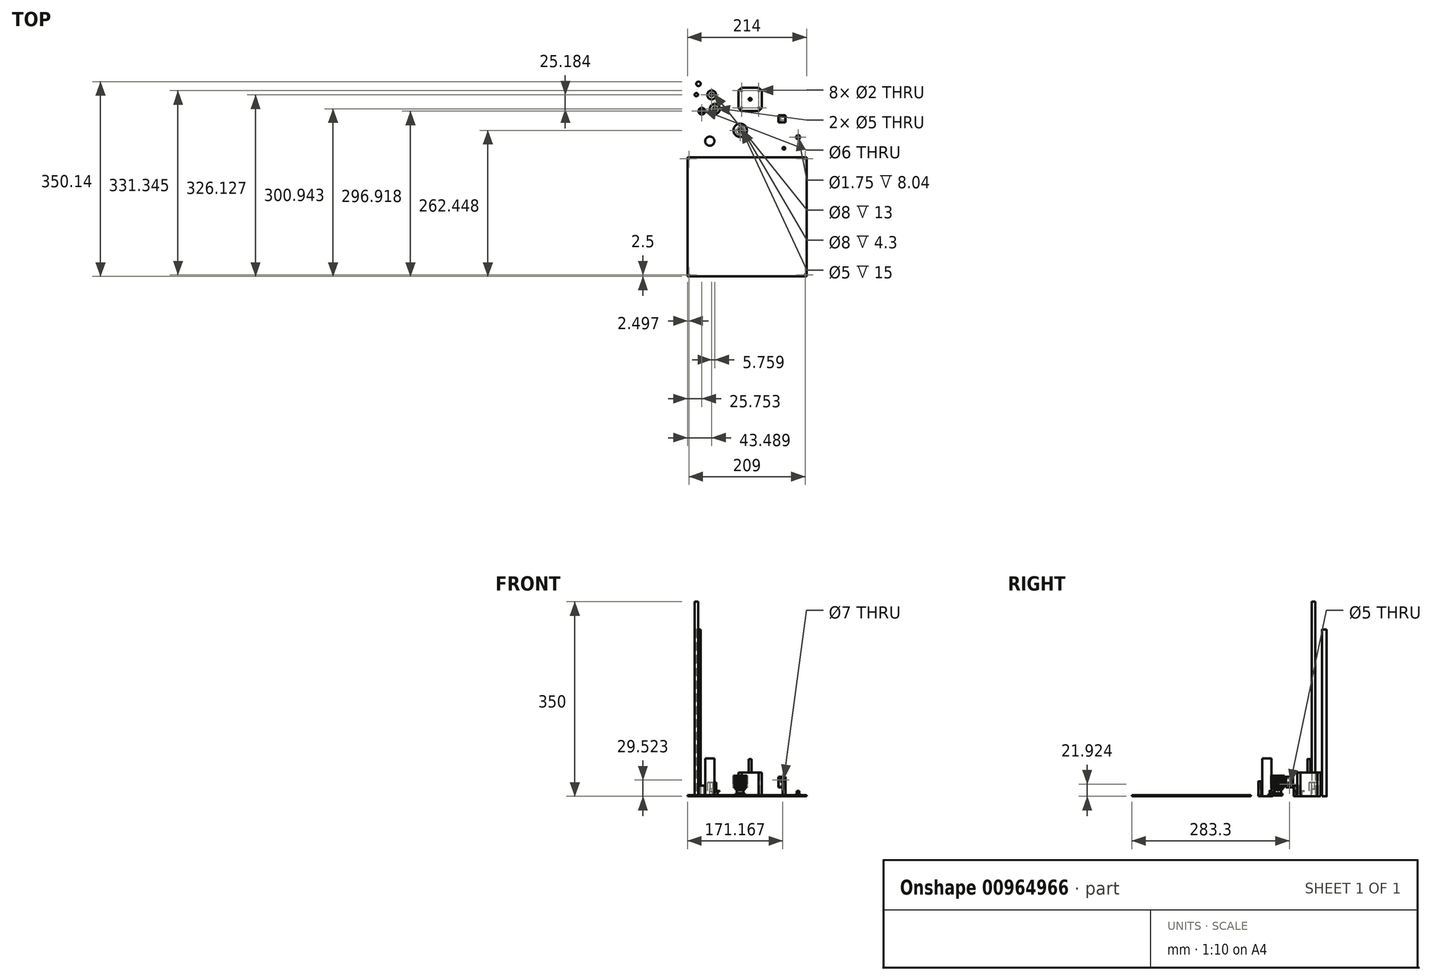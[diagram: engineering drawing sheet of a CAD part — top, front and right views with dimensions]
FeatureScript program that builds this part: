
annotation { "Feature Type Name" : "Feature", "Feature Type Description" : "" }
export const myFeature = defineFeature(function(context is Context, id is Id, definition is map)
    precondition{}
    {
        {
            var Q0;
            Q0=qCreatedBy(makeId("Top.planeOp"),FACE);
            var sketch = newSketch(context, id + "F0", { "sketchPlane" : qUnion([Q0])});
            skCircle(sketch, "E0", {"center": v(-57.26, 36.88) * mm, "radius": 3 * mm});
            skSolve(sketch);
        }
        {
            var Q0;
            Q0=makeQuery(id+"F0.imprint","IMPRINT",FACE,{"disambiguationData":[TD([[makeQuery(id+"F0.imprint","IMPRINT",EDGE,{"derivedFrom":sQuery(id+"F0.wireOp",EDGE,"E0")}),1.0]])]});
            extrude(context, id + "F1", {"entities" : qUnion([Q0]), "depth" : 350 * mm, "offsetDistance" : 25 * mm});
        }
        {
            var Q0;
            Q0=qCreatedBy(makeId("Top.planeOp"),FACE);
            var sketch = newSketch(context, id + "F2", { "sketchPlane" : qUnion([Q0])});
            skCircle(sketch, "E1", {"center": v(-29.78, 36.48) * mm, "radius": 4 * mm});
            skCircle(sketch, "E2", {"center": v(-29.78, 36.48) * mm, "radius": 8 * mm});
            skSolve(sketch);
        }
        {
            var Q0;
            Q0=makeQuery(id+"F2.imprint","IMPRINT",FACE,{"disambiguationData":[TD([[makeQuery(id+"F2.imprint","IMPRINT",EDGE,{"derivedFrom":sQuery(id+"F2.wireOp",EDGE,"E1")}),-1.0]])]});
            extrude(context, id + "F3", {"entities" : qUnion([Q0]), "depth" : 25 * mm, "offsetDistance" : 25 * mm});
        }
        {
            var Q0;
            Q0=qCreatedBy(makeId("Top.planeOp"),FACE);
            var sketch = newSketch(context, id + "F4", { "sketchPlane" : qUnion([Q0])});
            skCircle(sketch, "E3", {"center": v(-47.52, 7.27) * mm, "radius": 3 * mm});
            skCircle(sketch, "E4", {"center": v(-47.52, 7.27) * mm, "radius": 6 * mm});
            skSolve(sketch);
        }
        {
            var Q0;
            Q0=makeQuery(id+"F4.imprint","IMPRINT",FACE,{"disambiguationData":[TD([[makeQuery(id+"F4.imprint","IMPRINT",EDGE,{"derivedFrom":sQuery(id+"F4.wireOp",EDGE,"E3")}),-1.0]])]});
            extrude(context, id + "F5", {"entities" : qUnion([Q0]), "depth" : 19 * mm, "offsetDistance" : 25 * mm});
        }
        {
            var Q0;
            Q0=qCreatedBy(makeId("Top.planeOp"),FACE);
            var sketch = newSketch(context, id + "F6", { "sketchPlane" : qUnion([Q0])});
            skCircle(sketch, "E5", {"center": v(-24.02, 11.3) * mm, "radius": 5 * mm});
            skSolve(sketch);
        }
        {
            var Q0;
            Q0 = qSketchRegion(id + "F6", true);
            extrude(context, id + "F7", {"entities" : qUnion([Q0]), "depth" : 10 * mm, "offsetDistance" : 25 * mm});
        }
        {
            var Q0;
            Q0=makeQuery(id+"F7.opExtrude","CAP_FACE",FACE,{"disambiguationData":[OSD([sQuery(id+"F6.wireOp",EDGE,"E5")])],"isStart":false});
            var sketch = newSketch(context, id + "F8", { "sketchPlane" : qUnion([Q0])});
            skCircle(sketch, "E6", {"center": v(-24.02, 11.3) * mm, "radius": 5 * mm});
            skPoint(sketch, "E6.first.point", {"position": v(-22.8, 16.14) * mm});
            skPoint(sketch, "E6.second.point", {"position": v(-28.66, 13.17) * mm});
            skPoint(sketch, "E6.third.point", {"position": v(-23.1, 6.38) * mm});
            skCircle(sketch, "E7", {"center": v(-24.02, 11.3) * mm, "radius": 9 * mm});
            skSolve(sketch);
        }
        {
            var Q0;
            Q0 = qSketchRegion(id + "F8", true);
            extrude(context, id + "F9", {"entities" : qUnion([Q0]), "operationType" : NewBodyOperationType.ADD, "oppositeDirection" : true, "depth" : 1 * mm, "offsetDistance" : 25 * mm});
        }
        {
            var Q0;
            Q0=makeQuery(id+"F7.opExtrude","CAP_FACE",FACE,{"disambiguationData":[OSD([sQuery(id+"F6.wireOp",EDGE,"E5")])],"isStart":true});
            var sketch = newSketch(context, id + "F10", { "sketchPlane" : qUnion([Q0])});
            skPoint(sketch, "E8.first.point", {"position": v(-20.18, -8.1) * mm});
            skPoint(sketch, "E8.second.point", {"position": v(-24.93, -6.38) * mm});
            skPoint(sketch, "E8.third.point", {"position": v(-24.94, -16.4) * mm});
            skCircle(sketch, "E9", {"center": v(-24.06, -11.38) * mm, "radius": 9 * mm});
            skSolve(sketch);
        }
        {
            var Q0;
            Q0 = qSketchRegion(id + "F10", true);
            extrude(context, id + "F11", {"entities" : qUnion([Q0]), "operationType" : NewBodyOperationType.ADD, "oppositeDirection" : true, "depth" : 1 * mm, "offsetDistance" : 25 * mm});
        }
        {
            var Q0;
            Q0=qCreatedBy(makeId("Top.planeOp"),FACE);
            var sketch = newSketch(context, id + "F12", { "sketchPlane" : qUnion([Q0])});
            skLineSegment(sketch, "E10.bottom", {"start": v(23.86, 49.7) * mm, "end": v(54.86, 49.7) * mm});
            skLineSegment(sketch, "E10.top", {"start": v(23.86, 7.7) * mm, "end": v(54.86, 7.7) * mm});
            skLineSegment(sketch, "E11", {"start": v(38.86, 49.7) * mm, "end": v(54.86, 49.7) * mm, "construction": true});
            skLineSegment(sketch, "E12", {"start": v(38.86, 49.7) * mm, "end": v(23.86, 49.7) * mm, "construction": true});
            skLineSegment(sketch, "E13", {"start": v(23.86, 49.7) * mm, "end": v(23.86, 7.7) * mm, "construction": true});
            skLineSegment(sketch, "E14", {"start": v(23.86, 7.7) * mm, "end": v(54.86, 7.7) * mm, "construction": true});
            skLineSegment(sketch, "E15", {"start": v(54.86, 7.7) * mm, "end": v(54.86, 49.7) * mm, "construction": true});
            skLineSegment(sketch, "E16", {"start": v(54.86, 49.7) * mm, "end": v(54.86, 44.2) * mm, "construction": true});
            skLineSegment(sketch, "E17", {"start": v(54.86, 44.2) * mm, "end": v(60.36, 44.2) * mm, "construction": true});
            skLineSegment(sketch, "E18", {"start": v(60.36, 44.2) * mm, "end": v(18.36, 44.2) * mm, "construction": true});
            skLineSegment(sketch, "E19", {"start": v(18.36, 13.2) * mm, "end": v(60.36, 13.2) * mm, "construction": true});
            skCircle(sketch, "E20", {"center": v(23.86, 44.2) * mm, "radius": 1 * mm});
            skLineSegment(sketch, "E21", {"start": v(23.86, 49.7) * mm, "end": v(18.36, 44.2) * mm});
            skLineSegment(sketch, "E22", {"start": v(54.86, 49.7) * mm, "end": v(60.36, 44.2) * mm});
            skLineSegment(sketch, "E23", {"start": v(60.36, 13.2) * mm, "end": v(54.86, 7.7) * mm});
            skLineSegment(sketch, "E24", {"start": v(18.36, 13.2) * mm, "end": v(23.86, 7.7) * mm});
            skCircle(sketch, "E25", {"center": v(23.86, 13.2) * mm, "radius": 1 * mm});
            skCircle(sketch, "E26", {"center": v(54.86, 13.2) * mm, "radius": 1 * mm});
            skCircle(sketch, "E27", {"center": v(54.86, 44.2) * mm, "radius": 1 * mm});
            skPoint(sketch, "E28.orphan", {"position": v(18.36, 49.7) * mm});
            skPoint(sketch, "E29.orphan", {"position": v(59.36, 49.7) * mm});
            skPoint(sketch, "E30.orphan", {"position": v(59.36, 7.7) * mm});
            skPoint(sketch, "E31.orphan", {"position": v(18.36, 7.7) * mm});
            skLineSegment(sketch, "E32", {"start": v(18.36, 44.2) * mm, "end": v(18.36, 13.2) * mm});
            skLineSegment(sketch, "E33", {"start": v(60.36, 44.2) * mm, "end": v(60.36, 13.2) * mm});
            skLineSegment(sketch, "E34", {"start": v(23.86, 44.2) * mm, "end": v(54.86, 44.2) * mm, "construction": true});
            skLineSegment(sketch, "E35", {"start": v(23.86, 44.2) * mm, "end": v(18.36, 44.2) * mm, "construction": true});
            skLineSegment(sketch, "E36", {"start": v(23.86, 44.2) * mm, "end": v(23.86, 49.7) * mm, "construction": true});
            skLineSegment(sketch, "E37", {"start": v(23.86, 13.2) * mm, "end": v(18.36, 13.2) * mm, "construction": true});
            skLineSegment(sketch, "E38", {"start": v(23.86, 13.2) * mm, "end": v(23.86, 7.7) * mm, "construction": true});
            skLineSegment(sketch, "E39", {"start": v(54.86, 13.2) * mm, "end": v(23.86, 13.2) * mm, "construction": true});
            skLineSegment(sketch, "E40", {"start": v(54.86, 44.2) * mm, "end": v(23.86, 13.2) * mm, "construction": true});
            skCircle(sketch, "E41", {"center": v(39.36, 28.7) * mm, "radius": 2.5 * mm});
            skSolve(sketch);
        }
        {
            var Q0;
            Q0=makeQuery(id+"F12.imprint","IMPRINT",FACE,{"disambiguationData":[TD([[makeQuery(id+"F12.imprint","IMPRINT",EDGE,{"derivedFrom":sQuery(id+"F12.wireOp",EDGE,"E10.bottom")}),-1.0]])]});
            extrude(context, id + "F13", {"entities" : qUnion([Q0]), "depth" : 43 * mm, "offsetDistance" : 25 * mm});
        }
        {
            var Q0;
            Q0=makeQuery(id+"F12.imprint","IMPRINT",FACE,{"disambiguationData":[TD([[makeQuery(id+"F12.imprint","IMPRINT",EDGE,{"derivedFrom":sQuery(id+"F12.wireOp",EDGE,"E41")}),1.0]])]});
            extrude(context, id + "F14", {"entities" : qUnion([Q0]), "operationType" : NewBodyOperationType.ADD, "depth" : (42 + 25) * mm, "offsetDistance" : 25 * mm});
        }
        {
            var Q0;
            Q0=makeQuery(id+"F3.opExtrude","CAP_FACE",FACE,{"disambiguationData":[OSD([sQuery(id+"F2.wireOp",EDGE,"E1"),sQuery(id+"F2.wireOp",EDGE,"E2")])],"isStart":false});
            var sketch = newSketch(context, id + "F15", { "sketchPlane" : qUnion([Q0])});
            skCircle(sketch, "E42", {"center": v(-29.78, 36.48) * mm, "radius": 2.5 * mm});
            skSolve(sketch);
        }
        {
            var Q0;
            Q0=makeQuery(id+"F15.imprint","IMPRINT",FACE,{"disambiguationData":[TD([[makeQuery(id+"F15.imprint","IMPRINT",EDGE,{"derivedFrom":sQuery(id+"F15.wireOp",EDGE,"E42")}),-1.0]])]});
            extrude(context, id + "F16", {"entities" : qUnion([Q0]), "operationType" : NewBodyOperationType.ADD, "oppositeDirection" : true, "depth" : 12 * mm, "offsetDistance" : 25 * mm});
        }
        {
            var Q0;
            Q0=qCreatedBy(makeId("Top.planeOp"),FACE);
            var sketch = newSketch(context, id + "F17", { "sketchPlane" : qUnion([Q0])});
            skCircle(sketch, "E43", {"center": v(-53.53, 56.49) * mm, "radius": 4 * mm});
            skSolve(sketch);
        }
        {
            var Q0;
            Q0 = qSketchRegion(id + "F17", true);
            extrude(context, id + "F18", {"entities" : qUnion([Q0]), "depth" : 300 * mm, "offsetDistance" : 25 * mm});
        }
        {
            var Q0;
            Q0=qCreatedBy(makeId("Top.planeOp"),FACE);
            var sketch = newSketch(context, id + "F19", { "sketchPlane" : qUnion([Q0])});
            skLineSegment(sketch, "E44.bottom", {"start": v(-73.27, -75.65) * mm, "end": v(140.73, -75.65) * mm});
            skLineSegment(sketch, "E44.top", {"start": v(-73.27, -289.65) * mm, "end": v(140.73, -289.65) * mm});
            skLineSegment(sketch, "E44.left", {"start": v(-73.27, -75.65) * mm, "end": v(-73.27, -289.65) * mm});
            skLineSegment(sketch, "E44.right", {"start": v(140.73, -75.65) * mm, "end": v(140.73, -289.65) * mm});
            skLineSegment(sketch, "E45", {"start": v(-73.27, -75.65) * mm, "end": v(140.73, -289.65) * mm, "construction": true});
            skLineSegment(sketch, "E46.bottom", {"start": v(138.23, -78.15) * mm, "end": v(-70.77, -78.15) * mm, "construction": true});
            skLineSegment(sketch, "E46.top", {"start": v(138.23, -287.15) * mm, "end": v(-70.77, -287.15) * mm, "construction": true});
            skLineSegment(sketch, "E46.left", {"start": v(138.23, -78.15) * mm, "end": v(138.23, -287.15) * mm, "construction": true});
            skLineSegment(sketch, "E46.right", {"start": v(-70.77, -78.15) * mm, "end": v(-70.77, -287.15) * mm, "construction": true});
            skPoint(sketch, "E46.middle", {"position": v(33.73, -182.65) * mm});
            skCircle(sketch, "E47", {"center": v(-70.77, -78.15) * mm, "radius": 1 * mm});
            skCircle(sketch, "E48", {"center": v(138.23, -78.15) * mm, "radius": 1 * mm});
            skCircle(sketch, "E49", {"center": v(138.23, -287.15) * mm, "radius": 1 * mm});
            skCircle(sketch, "E50", {"center": v(-70.77, -287.15) * mm, "radius": 1 * mm});
            skSolve(sketch);
        }
        {
            var Q0;
            Q0=makeQuery(id+"F19.imprint","IMPRINT",FACE,{"disambiguationData":[TD([[makeQuery(id+"F19.imprint","IMPRINT",EDGE,{"derivedFrom":sQuery(id+"F19.wireOp",EDGE,"E44.bottom")}),-1.0]])]});
            extrude(context, id + "F20", {"entities" : qUnion([Q0]), "depth" : 2 * mm, "offsetDistance" : 25 * mm});
        }
        {
            var Q0;
            Q0=qCreatedBy(makeId("Top.planeOp"),FACE);
            var sketch = newSketch(context, id + "F21", { "sketchPlane" : qUnion([Q0])});
            skCircle(sketch, "E51", {"center": v(-33.14, -46.66) * mm, "radius": 8.25 * mm});
            skSolve(sketch);
        }
        {
            var Q0;
            Q0=makeQuery(id+"F21.imprint","IMPRINT",FACE,{"disambiguationData":[TD([[makeQuery(id+"F21.imprint","IMPRINT",EDGE,{"derivedFrom":sQuery(id+"F21.wireOp",EDGE,"E51")}),1.0]])]});
            extrude(context, id + "F22", {"entities" : qUnion([Q0]), "depth" : 68 * mm, "offsetDistance" : 25 * mm});
        }
        {
            var Q0;
            Q0=qCreatedBy(makeId("Top.planeOp"),FACE);
            var sketch = newSketch(context, id + "F23", { "sketchPlane" : qUnion([Q0])});
            skCircle(sketch, "E52", {"center": v(21.49, -27.2) * mm, "radius": 2 * mm});
            skSolve(sketch);
        }
        {
            var Q0;
            Q0 = qSketchRegion(id + "F23", true);
            extrude(context, id + "F24", {"entities" : qUnion([Q0]), "depth" : 1.7 * mm, "offsetDistance" : 25 * mm});
        }
        {
            var Q0;
            Q0=makeQuery(id+"F24.opExtrude","CAP_FACE",FACE,{"disambiguationData":[OSD([sQuery(id+"F23.wireOp",EDGE,"E52")])],"isStart":false});
            var sketch = newSketch(context, id + "F25", { "sketchPlane" : qUnion([Q0])});
            skCircle(sketch, "E53", {"center": v(21.49, -27.2) * mm, "radius": 8 * mm});
            skSolve(sketch);
        }
        {
            var Q0;
            Q0=makeQuery(id+"F25.imprint","IMPRINT",FACE,{"disambiguationData":[TD([[makeQuery(id+"F25.imprint","IMPRINT",EDGE,{"derivedFrom":sQuery(id+"F25.wireOp",EDGE,"E53")}),1.0]])]});
            var Q1;
            Q1=makeQuery(id+"F25.imprint","IMPRINT",FACE,{"disambiguationData":[TD([[makeQuery(id+"F25.imprint","IMPRINT",EDGE,{"derivedFrom":makeQuery(id+"F24.opExtrude","CAP_EDGE",EDGE,{"disambiguationData":[OSD([sQuery(id+"F23.wireOp",EDGE,"E52")])],"isStart":false})}),1.0]])]});
            extrude(context, id + "F26", {"entities" : qUnion([Q0, Q1]), "operationType" : NewBodyOperationType.ADD, "depth" : 3.7 * mm, "offsetDistance" : 25 * mm});
        }
        {
            var Q0;
            Q0=makeQuery(id+"F26.opExtrude","CAP_FACE",FACE,{"disambiguationData":[OSD([sQuery(id+"F25.wireOp",EDGE,"E53")])],"isStart":false});
            var sketch = newSketch(context, id + "F27", { "sketchPlane" : qUnion([Q0])});
            skCircle(sketch, "E54", {"center": v(21.49, -27.2) * mm, "radius": 6 * mm});
            skSolve(sketch);
        }
        {
            var Q0;
            Q0=makeQuery(id+"F27.imprint","IMPRINT",FACE,{"disambiguationData":[TD([[makeQuery(id+"F27.imprint","IMPRINT",EDGE,{"derivedFrom":sQuery(id+"F27.wireOp",EDGE,"E54")}),1.0]])]});
            extrude(context, id + "F28", {"entities" : qUnion([Q0]), "operationType" : NewBodyOperationType.ADD, "depth" : 6 * mm, "offsetDistance" : 25 * mm});
        }
        {
            var Q0;
            Q0=makeQuery(id+"F28.opExtrude","CAP_FACE",FACE,{"disambiguationData":[OSD([sQuery(id+"F27.wireOp",EDGE,"E54")])],"isStart":false});
            var sketch = newSketch(context, id + "F29", { "sketchPlane" : qUnion([Q0])});
            skCircle(sketch, "E55", {"center": v(21.49, -27.2) * mm, "radius": 8 * mm});
            skSolve(sketch);
        }
        {
            var Q0;
            Q0=makeQuery(id+"F29.imprint","IMPRINT",FACE,{"disambiguationData":[TD([[makeQuery(id+"F29.imprint","IMPRINT",EDGE,{"derivedFrom":makeQuery(id+"F28.opExtrude","CAP_EDGE",EDGE,{"disambiguationData":[OSD([sQuery(id+"F27.wireOp",EDGE,"E54")])],"isStart":false})}),1.0]])]});
            var Q1;
            Q1=makeQuery(id+"F29.imprint","IMPRINT",FACE,{"disambiguationData":[TD([[makeQuery(id+"F29.imprint","IMPRINT",EDGE,{"derivedFrom":sQuery(id+"F29.wireOp",EDGE,"E55")}),1.0]])]});
            extrude(context, id + "F30", {"entities" : qUnion([Q0, Q1]), "operationType" : NewBodyOperationType.ADD, "depth" : 3 * mm, "offsetDistance" : 25 * mm});
        }
        {
            var Q0;
            Q0=makeQuery(id+"F24.opExtrude","CAP_FACE",FACE,{"disambiguationData":[OSD([sQuery(id+"F23.wireOp",EDGE,"E52")])],"isStart":true});
            var sketch = newSketch(context, id + "F31", { "sketchPlane" : qUnion([Q0])});
            skCircle(sketch, "E56", {"center": v(21.49, 27.2) * mm, "radius": 4 * mm});
            skSolve(sketch);
        }
        {
            var Q0;
            Q0 = qSketchRegion(id + "F31", true);
            extrude(context, id + "F32", {"entities" : qUnion([Q0]), "operationType" : NewBodyOperationType.REMOVE, "oppositeDirection" : true, "depth" : 6 * mm, "offsetDistance" : 25 * mm});
        }
        {
            var Q0;
            Q0=makeQuery(id+"F30.opExtrude","CAP_FACE",FACE,{"disambiguationData":[OSD([sQuery(id+"F29.wireOp",EDGE,"E55")])],"isStart":false});
            var sketch = newSketch(context, id + "F33", { "sketchPlane" : qUnion([Q0])});
            skCircle(sketch, "E57", {"center": v(21.49, -27.2) * mm, "radius": 5 * mm});
            skSolve(sketch);
        }
        {
            var Q0;
            Q0 = qSketchRegion(id + "F33", true);
            extrude(context, id + "F34", {"entities" : qUnion([Q0]), "operationType" : NewBodyOperationType.ADD, "depth" : 1.5 * mm, "offsetDistance" : 25 * mm});
        }
        {
            var Q0;
            Q0=makeQuery(id+"F34.opExtrude","CAP_FACE",FACE,{"disambiguationData":[OSD([sQuery(id+"F33.wireOp",EDGE,"E57")])],"isStart":false});
            var sketch = newSketch(context, id + "F35", { "sketchPlane" : qUnion([Q0])});
            skCircle(sketch, "E58", {"center": v(21.49, -27.2) * mm, "radius": 12 * mm});
            skSolve(sketch);
        }
        {
            var Q0;
            Q0 = qSketchRegion(id + "F35", true);
            extrude(context, id + "F36", {"entities" : qUnion([Q0]), "operationType" : NewBodyOperationType.ADD, "depth" : 1 * mm, "offsetDistance" : 25 * mm});
        }
        {
            var Q0;
            Q0=makeQuery(id+"F36.opExtrude","CAP_FACE",FACE,{"disambiguationData":[OSD([sQuery(id+"F35.wireOp",EDGE,"E58")])],"isStart":false});
            var sketch = newSketch(context, id + "F37", { "sketchPlane" : qUnion([Q0])});
            skCircle(sketch, "E59", {"center": v(21.49, -27.2) * mm, "radius": 5 * mm});
            skSolve(sketch);
        }
        {
            var Q0;
            Q0=makeQuery(id+"F37.imprint","IMPRINT",FACE,{"disambiguationData":[TD([[makeQuery(id+"F37.imprint","IMPRINT",EDGE,{"derivedFrom":sQuery(id+"F37.wireOp",EDGE,"E59")}),1.0]])]});
            extrude(context, id + "F38", {"entities" : qUnion([Q0]), "operationType" : NewBodyOperationType.ADD, "depth" : 1.5 * mm, "offsetDistance" : 25 * mm});
        }
        {
            var Q0;
            Q0=makeQuery(id+"F38.opExtrude","CAP_FACE",FACE,{"disambiguationData":[OSD([sQuery(id+"F37.wireOp",EDGE,"E59")])],"isStart":false});
            var sketch = newSketch(context, id + "F39", { "sketchPlane" : qUnion([Q0])});
            skCircle(sketch, "E60", {"center": v(21.49, -27.2) * mm, "radius": 12 * mm});
            skSolve(sketch);
        }
        {
            var Q0;
            Q0 = qSketchRegion(id + "F39", true);
            extrude(context, id + "F40", {"entities" : qUnion([Q0]), "operationType" : NewBodyOperationType.ADD, "depth" : 1 * mm, "offsetDistance" : 25 * mm});
        }
        {
            var Q0;
            Q0=makeQuery(id+"F40.opExtrude","CAP_FACE",FACE,{"disambiguationData":[OSD([sQuery(id+"F39.wireOp",EDGE,"E60")])],"isStart":false});
            var sketch = newSketch(context, id + "F41", { "sketchPlane" : qUnion([Q0])});
            skCircle(sketch, "E61", {"center": v(21.49, -27.2) * mm, "radius": 5 * mm});
            skSolve(sketch);
        }
        {
            var Q0;
            Q0=makeQuery(id+"F41.imprint","IMPRINT",FACE,{"disambiguationData":[TD([[makeQuery(id+"F41.imprint","IMPRINT",EDGE,{"derivedFrom":sQuery(id+"F41.wireOp",EDGE,"E61")}),1.0]])]});
            extrude(context, id + "F42", {"entities" : qUnion([Q0]), "operationType" : NewBodyOperationType.ADD, "depth" : 1.5 * mm, "offsetDistance" : 25 * mm});
        }
        {
            var Q0;
            Q0=makeQuery(id+"F42.opExtrude","CAP_FACE",FACE,{"disambiguationData":[OSD([sQuery(id+"F41.wireOp",EDGE,"E61")])],"isStart":false});
            var sketch = newSketch(context, id + "F43", { "sketchPlane" : qUnion([Q0])});
            skCircle(sketch, "E62", {"center": v(21.49, -27.2) * mm, "radius": 12 * mm});
            skSolve(sketch);
        }
        {
            var Q0;
            Q0 = qSketchRegion(id + "F43", true);
            extrude(context, id + "F44", {"entities" : qUnion([Q0]), "operationType" : NewBodyOperationType.ADD, "depth" : 1 * mm, "offsetDistance" : 25 * mm});
        }
        {
            var Q0;
            Q0=makeQuery(id+"F44.opExtrude","CAP_FACE",FACE,{"disambiguationData":[OSD([sQuery(id+"F43.wireOp",EDGE,"E62")])],"isStart":false});
            var sketch = newSketch(context, id + "F45", { "sketchPlane" : qUnion([Q0])});
            skCircle(sketch, "E63", {"center": v(21.49, -27.2) * mm, "radius": 5.5 * mm});
            skSolve(sketch);
        }
        {
            var Q0;
            Q0 = qSketchRegion(id + "F45", true);
            extrude(context, id + "F46", {"entities" : qUnion([Q0]), "operationType" : NewBodyOperationType.ADD, "depth" : 1.5 * mm, "offsetDistance" : 25 * mm});
        }
        {
            var Q0;
            Q0=makeQuery(id+"F46.opExtrude","CAP_FACE",FACE,{"disambiguationData":[OSD([sQuery(id+"F45.wireOp",EDGE,"E63")])],"isStart":false});
            var sketch = newSketch(context, id + "F47", { "sketchPlane" : qUnion([Q0])});
            skCircle(sketch, "E64", {"center": v(21.49, -27.2) * mm, "radius": 12 * mm});
            skSolve(sketch);
        }
        {
            var Q0;
            Q0 = qSketchRegion(id + "F47", true);
            extrude(context, id + "F48", {"entities" : qUnion([Q0]), "operationType" : NewBodyOperationType.ADD, "depth" : 1 * mm, "offsetDistance" : 25 * mm});
        }
        {
            var Q0;
            Q0=makeQuery(id+"F48.opExtrude","CAP_FACE",FACE,{"disambiguationData":[OSD([sQuery(id+"F47.wireOp",EDGE,"E64")])],"isStart":false});
            var sketch = newSketch(context, id + "F49", { "sketchPlane" : qUnion([Q0])});
            skCircle(sketch, "E65", {"center": v(21.49, -27.2) * mm, "radius": 5.5 * mm});
            skSolve(sketch);
        }
        {
            var Q0;
            Q0 = qSketchRegion(id + "F49", true);
            extrude(context, id + "F50", {"entities" : qUnion([Q0]), "operationType" : NewBodyOperationType.ADD, "depth" : 1.5 * mm, "offsetDistance" : 25 * mm});
        }
        {
            var Q0;
            Q0=makeQuery(id+"F50.opExtrude","CAP_FACE",FACE,{"disambiguationData":[OSD([sQuery(id+"F49.wireOp",EDGE,"E65")])],"isStart":false});
            var sketch = newSketch(context, id + "F51", { "sketchPlane" : qUnion([Q0])});
            skCircle(sketch, "E66", {"center": v(21.49, -27.2) * mm, "radius": 12 * mm});
            skSolve(sketch);
        }
        {
            var Q0;
            Q0 = qSketchRegion(id + "F51", true);
            extrude(context, id + "F52", {"entities" : qUnion([Q0]), "operationType" : NewBodyOperationType.ADD, "depth" : 1 * mm, "offsetDistance" : 25 * mm});
        }
        {
            var Q0;
            Q0=makeQuery(id+"F52.opExtrude","CAP_FACE",FACE,{"disambiguationData":[OSD([sQuery(id+"F51.wireOp",EDGE,"E66")])],"isStart":false});
            var sketch = newSketch(context, id + "F53", { "sketchPlane" : qUnion([Q0])});
            skCircle(sketch, "E67", {"center": v(21.49, -27.2) * mm, "radius": 5.5 * mm});
            skSolve(sketch);
        }
        {
            var Q0;
            Q0 = qSketchRegion(id + "F53", true);
            extrude(context, id + "F54", {"entities" : qUnion([Q0]), "operationType" : NewBodyOperationType.ADD, "depth" : 1.5 * mm, "offsetDistance" : 25 * mm});
        }
        {
            var Q0;
            Q0=makeQuery(id+"F54.opExtrude","CAP_FACE",FACE,{"disambiguationData":[OSD([sQuery(id+"F53.wireOp",EDGE,"E67")])],"isStart":false});
            var sketch = newSketch(context, id + "F55", { "sketchPlane" : qUnion([Q0])});
            skCircle(sketch, "E68", {"center": v(21.49, -27.2) * mm, "radius": 12 * mm});
            skSolve(sketch);
        }
        {
            var Q0;
            Q0 = qSketchRegion(id + "F55", true);
            extrude(context, id + "F56", {"entities" : qUnion([Q0]), "operationType" : NewBodyOperationType.ADD, "depth" : 1 * mm, "offsetDistance" : 25 * mm});
        }
        {
            var Q0;
            Q0=makeQuery(id+"F56.opExtrude","CAP_FACE",FACE,{"disambiguationData":[OSD([sQuery(id+"F55.wireOp",EDGE,"E68")])],"isStart":false});
            var sketch = newSketch(context, id + "F57", { "sketchPlane" : qUnion([Q0])});
            skCircle(sketch, "E69", {"center": v(21.49, -27.2) * mm, "radius": 5.5 * mm});
            skSolve(sketch);
        }
        {
            var Q0;
            Q0 = qSketchRegion(id + "F57", true);
            extrude(context, id + "F58", {"entities" : qUnion([Q0]), "operationType" : NewBodyOperationType.ADD, "depth" : 1.5 * mm, "offsetDistance" : 25 * mm});
        }
        {
            var Q0;
            Q0=makeQuery(id+"F58.opExtrude","CAP_FACE",FACE,{"disambiguationData":[OSD([sQuery(id+"F57.wireOp",EDGE,"E69")])],"isStart":false});
            var sketch = newSketch(context, id + "F59", { "sketchPlane" : qUnion([Q0])});
            skCircle(sketch, "E70", {"center": v(21.49, -27.2) * mm, "radius": 12 * mm});
            skSolve(sketch);
        }
        {
            var Q0;
            Q0 = qSketchRegion(id + "F59", true);
            extrude(context, id + "F60", {"entities" : qUnion([Q0]), "operationType" : NewBodyOperationType.ADD, "depth" : 1 * mm, "offsetDistance" : 25 * mm});
        }
        {
            var Q0;
            Q0=makeQuery(id+"F60.opExtrude","CAP_FACE",FACE,{"disambiguationData":[OSD([sQuery(id+"F59.wireOp",EDGE,"E70")])],"isStart":false});
            var sketch = newSketch(context, id + "F61", { "sketchPlane" : qUnion([Q0])});
            skCircle(sketch, "E71", {"center": v(21.49, -27.2) * mm, "radius": 5.5 * mm});
            skSolve(sketch);
        }
        {
            var Q0;
            Q0=makeQuery(id+"F61.imprint","IMPRINT",FACE,{"disambiguationData":[TD([[makeQuery(id+"F61.imprint","IMPRINT",EDGE,{"derivedFrom":sQuery(id+"F61.wireOp",EDGE,"E71")}),1.0]])]});
            extrude(context, id + "F62", {"entities" : qUnion([Q0]), "operationType" : NewBodyOperationType.ADD, "depth" : 1.5 * mm, "offsetDistance" : 25 * mm});
        }
        {
            var Q0;
            Q0=makeQuery(id+"F62.opExtrude","CAP_FACE",FACE,{"disambiguationData":[OSD([sQuery(id+"F61.wireOp",EDGE,"E71")])],"isStart":false});
            var sketch = newSketch(context, id + "F63", { "sketchPlane" : qUnion([Q0])});
            skCircle(sketch, "E72", {"center": v(21.49, -27.2) * mm, "radius": 12 * mm});
            skSolve(sketch);
        }
        {
            var Q0;
            Q0 = qSketchRegion(id + "F63", true);
            extrude(context, id + "F64", {"entities" : qUnion([Q0]), "operationType" : NewBodyOperationType.ADD, "depth" : 1 * mm, "offsetDistance" : 25 * mm});
        }
        {
            var Q0;
            Q0=makeQuery(id+"F64.opExtrude","CAP_FACE",FACE,{"disambiguationData":[OSD([sQuery(id+"F63.wireOp",EDGE,"E72")])],"isStart":false});
            var sketch = newSketch(context, id + "F65", { "sketchPlane" : qUnion([Q0])});
            skCircle(sketch, "E73", {"center": v(21.49, -27.2) * mm, "radius": 5.5 * mm});
            skSolve(sketch);
        }
        {
            var Q0;
            Q0 = qSketchRegion(id + "F65", true);
            var Q1;
            Q1=makeQuery(id+"F65.imprint","IMPRINT",FACE,{"disambiguationData":[TD([[makeQuery(id+"F65.imprint","IMPRINT",EDGE,{"derivedFrom":sQuery(id+"F65.wireOp",EDGE,"E73")}),1.0]])]});
            extrude(context, id + "F66", {"entities" : qUnion([Q0, Q1]), "operationType" : NewBodyOperationType.ADD, "depth" : 1.5 * mm, "offsetDistance" : 25 * mm});
        }
        {
            var Q0;
            Q0=makeQuery(id+"F66.opExtrude","CAP_FACE",FACE,{"disambiguationData":[OSD([sQuery(id+"F65.wireOp",EDGE,"E73")])],"isStart":false});
            var sketch = newSketch(context, id + "F67", { "sketchPlane" : qUnion([Q0])});
            skCircle(sketch, "E74", {"center": v(21.49, -27.2) * mm, "radius": 12 * mm});
            skSolve(sketch);
        }
        {
            var Q0;
            Q0=makeQuery(id+"F67.imprint","IMPRINT",FACE,{"disambiguationData":[TD([[makeQuery(id+"F67.imprint","IMPRINT",EDGE,{"derivedFrom":sQuery(id+"F67.wireOp",EDGE,"E74")}),1.0]])]});
            var Q1;
            Q1=makeQuery(id+"F67.imprint","IMPRINT",FACE,{"disambiguationData":[TD([[makeQuery(id+"F67.imprint","IMPRINT",EDGE,{"derivedFrom":makeQuery(id+"F66.opExtrude","CAP_EDGE",EDGE,{"disambiguationData":[OSD([sQuery(id+"F65.wireOp",EDGE,"E73")])],"isStart":false})}),1.0]])]});
            extrude(context, id + "F68", {"entities" : qUnion([Q0, Q1]), "operationType" : NewBodyOperationType.ADD, "depth" : 1 * mm, "offsetDistance" : 25 * mm});
        }
        {
            var Q0;
            Q0=makeQuery(id+"F32.boolean.opBoolean","COPY",FACE,{"derivedFrom":makeQuery(id+"F32.opExtrude","CAP_FACE",FACE,{"disambiguationData":[OSD([sQuery(id+"F31.wireOp",EDGE,"E56")])],"isStart":false})});
            var sketch = newSketch(context, id + "F69", { "sketchPlane" : qUnion([Q0])});
            skCircle(sketch, "E75", {"center": v(21.49, 27.2) * mm, "radius": 0.88 * mm});
            skSolve(sketch);
        }
        {
            var Q0;
            Q0=makeQuery(id+"F69.imprint","IMPRINT",FACE,{"disambiguationData":[TD([[makeQuery(id+"F69.imprint","IMPRINT",EDGE,{"derivedFrom":sQuery(id+"F69.wireOp",EDGE,"E75")}),1.0]])]});
            var Q1;
            Q1=sQuery(id+"F69.wireOp",EDGE,"E75");
            extrude(context, id + "F70", {"entities" : qUnion([Q0]), "operationType" : NewBodyOperationType.REMOVE, "surfaceEntities" : qUnion([Q1]), "oppositeDirection" : true, "depth" : 63 * mm, "offsetDistance" : 25 * mm});
        }
        {
            var Q0;
            Q0=makeQuery(id+"F68.opExtrude","CAP_FACE",FACE,{"disambiguationData":[OSD([sQuery(id+"F67.wireOp",EDGE,"E74")])],"isStart":false});
            var sketch = newSketch(context, id + "F71", { "sketchPlane" : qUnion([Q0])});
            skCircle(sketch, "E76", {"center": v(21.49, -27.2) * mm, "radius": 2.5 * mm});
            skSolve(sketch);
        }
        {
            var Q0;
            Q0=makeQuery(id+"F71.imprint","IMPRINT",FACE,{"disambiguationData":[TD([[makeQuery(id+"F71.imprint","IMPRINT",EDGE,{"derivedFrom":sQuery(id+"F71.wireOp",EDGE,"E76")}),1.0]])]});
            extrude(context, id + "F72", {"entities" : qUnion([Q0]), "operationType" : NewBodyOperationType.REMOVE, "oppositeDirection" : true, "depth" : 15 * mm, "offsetDistance" : 25 * mm});
        }
        {
            var Q0;
            Q0=qCreatedBy(makeId("Front.planeOp"),FACE);
            var sketch = newSketch(context, id + "F73", { "sketchPlane" : qUnion([Q0])});
            skLineSegment(sketch, "E77.bottom", {"start": v(102.9, 34.92) * mm, "end": v(90.2, 34.92) * mm});
            skLineSegment(sketch, "E77.top", {"start": v(102.9, 15.92) * mm, "end": v(90.2, 15.92) * mm});
            skLineSegment(sketch, "E77.left", {"start": v(102.9, 34.92) * mm, "end": v(102.9, 15.92) * mm});
            skLineSegment(sketch, "E77.right", {"start": v(90.2, 34.92) * mm, "end": v(90.2, 15.92) * mm});
            skLineSegment(sketch, "E78", {"start": v(102.9, 34.92) * mm, "end": v(97.9, 34.92) * mm, "construction": true});
            skLineSegment(sketch, "E79", {"start": v(97.9, 34.92) * mm, "end": v(97.9, 29.52) * mm, "construction": true});
            skCircle(sketch, "E80", {"center": v(97.9, 29.52) * mm, "radius": 3.5 * mm});
            skLineSegment(sketch, "E81", {"start": v(97.9, 29.52) * mm, "end": v(93.19, 29.52) * mm, "construction": true});
            skLineSegment(sketch, "E82", {"start": v(93.19, 29.52) * mm, "end": v(93.19, 32.61) * mm, "construction": true});
            skCircle(sketch, "E83", {"center": v(93.19, 32.61) * mm, "radius": 0.75 * mm});
            skSolve(sketch);
        }
        {
            var Q0;
            Q0=makeQuery(id+"F73.imprint","IMPRINT",FACE,{"disambiguationData":[TD([[makeQuery(id+"F73.imprint","IMPRINT",EDGE,{"derivedFrom":sQuery(id+"F73.wireOp",EDGE,"E77.bottom")}),1.0]])]});
            extrude(context, id + "F74", {"entities" : qUnion([Q0]), "depth" : 12.7 * mm, "offsetDistance" : 25 * mm});
        }
        {
            var Q0;
            Q0=makeQuery(id+"F74.opExtrude","SWEPT_FACE",FACE,{"disambiguationData":[OSD([sQuery(id+"F73.wireOp",EDGE,"E77.right")])]});
            var sketch = newSketch(context, id + "F75", { "sketchPlane" : qUnion([Q0])});
            skLineSegment(sketch, "E84", {"start": v(6.35, 34.92) * mm, "end": v(6.35, 15.92) * mm, "construction": true});
            skLineSegment(sketch, "E85", {"start": v(6.35, 15.92) * mm, "end": v(6.35, 21.92) * mm, "construction": true});
            skCircle(sketch, "E86", {"center": v(6.35, 21.92) * mm, "radius": 2.5 * mm});
            skSolve(sketch);
        }
        {
            var Q0;
            Q0=makeQuery(id+"F75.imprint","IMPRINT",FACE,{"disambiguationData":[TD([[makeQuery(id+"F75.imprint","IMPRINT",EDGE,{"derivedFrom":sQuery(id+"F75.wireOp",EDGE,"E86")}),1.0]])]});
            extrude(context, id + "F76", {"entities" : qUnion([Q0]), "operationType" : NewBodyOperationType.REMOVE, "oppositeDirection" : true, "depth" : 25 * mm, "offsetDistance" : 25 * mm});
        }
        {
            var Q0;
            Q0=qCreatedBy(makeId("Top.planeOp"),FACE);
            var sketch = newSketch(context, id + "F77", { "sketchPlane" : qUnion([Q0])});
            skCircle(sketch, "E87", {"center": v(125.37, -39.5) * mm, "radius": 0.1 * mm});
            skCircle(sketch, "E88.cCircle", {"center": v(125.37, -39.5) * mm, "radius": 3.5 * mm, "construction": true});
            skLineSegment(sketch, "E88.0", {"start": v(121.87, -41.52) * mm, "end": v(121.87, -37.47) * mm});
            skLineSegment(sketch, "E88.1", {"start": v(121.87, -37.47) * mm, "end": v(125.37, -35.45) * mm});
            skLineSegment(sketch, "E88.2", {"start": v(125.37, -35.45) * mm, "end": v(128.87, -37.47) * mm});
            skLineSegment(sketch, "E88.3", {"start": v(128.87, -37.47) * mm, "end": v(128.87, -41.52) * mm});
            skLineSegment(sketch, "E88.4", {"start": v(128.87, -41.52) * mm, "end": v(125.37, -43.54) * mm});
            skLineSegment(sketch, "E88.5", {"start": v(125.37, -43.54) * mm, "end": v(121.87, -41.52) * mm});
            skPoint(sketch, "E88.0.midPoint", {"position": v(121.87, -39.5) * mm});
            skSolve(sketch);
        }
        {
            var Q0;
            Q0=makeQuery(id+"F77.imprint","IMPRINT",FACE,{"disambiguationData":[TD([[makeQuery(id+"F77.imprint","IMPRINT",EDGE,{"derivedFrom":sQuery(id+"F77.wireOp",EDGE,"E87")}),-1.0]])]});
            extrude(context, id + "F78", {"entities" : qUnion([Q0]), "depth" : 5 * mm, "offsetDistance" : 25 * mm});
        }
        {
            var Q0;
            Q0=makeQuery(id+"F78.opExtrude","CAP_EDGE",EDGE,{"disambiguationData":[OSD([sQuery(id+"F77.wireOp",EDGE,"E88.1")])],"isStart":true});
            var Q1;
            Q1=makeQuery(id+"F78.opExtrude","CAP_EDGE",EDGE,{"disambiguationData":[OSD([sQuery(id+"F77.wireOp",EDGE,"E88.0")])],"isStart":true});
            var Q2;
            Q2=makeQuery(id+"F78.opExtrude","CAP_EDGE",EDGE,{"disambiguationData":[OSD([sQuery(id+"F77.wireOp",EDGE,"E88.2")])],"isStart":true});
            var Q3;
            Q3=makeQuery(id+"F78.opExtrude","CAP_EDGE",EDGE,{"disambiguationData":[OSD([sQuery(id+"F77.wireOp",EDGE,"E88.3")])],"isStart":true});
            var Q4;
            Q4=makeQuery(id+"F78.opExtrude","CAP_EDGE",EDGE,{"disambiguationData":[OSD([sQuery(id+"F77.wireOp",EDGE,"E88.4")])],"isStart":true});
            var Q5;
            Q5=makeQuery(id+"F78.opExtrude","CAP_EDGE",EDGE,{"disambiguationData":[OSD([sQuery(id+"F77.wireOp",EDGE,"E88.5")])],"isStart":true});
            fillet(context, id + "F79", {"entities" : qUnion([Q0, Q1, Q2, Q3, Q4, Q5]), "radius" : 3.19 * mm, "tangentPropagation" : true, "rho" : 0.5, "crossSection" : FilletCrossSection.CONIC, "allowEdgeOverflow" : false});
        }
        {
            var Q0;
            Q0=makeQuery(id+"F78.opExtrude","CAP_FACE",FACE,{"disambiguationData":[OSD([sQuery(id+"F77.wireOp",EDGE,"E87"),sQuery(id+"F77.wireOp",EDGE,"E88.0"),sQuery(id+"F77.wireOp",EDGE,"E88.1"),sQuery(id+"F77.wireOp",EDGE,"E88.2"),sQuery(id+"F77.wireOp",EDGE,"E88.3"),sQuery(id+"F77.wireOp",EDGE,"E88.4"),sQuery(id+"F77.wireOp",EDGE,"E88.5")])],"isStart":false});
            var sketch = newSketch(context, id + "F80", { "sketchPlane" : qUnion([Q0])});
            skCircle(sketch, "E89", {"center": v(125.37, -39.5) * mm, "radius": 0.88 * mm});
            skSolve(sketch);
        }
        {
            var Q0;
            Q0 = qSketchRegion(id + "F80", true);
            extrude(context, id + "F81", {"entities" : qUnion([Q0]), "operationType" : NewBodyOperationType.REMOVE, "oppositeDirection" : true, "depth" : 3.04 * mm, "offsetDistance" : 25 * mm});
        }
        {
            var Q0;
            Q0=makeQuery(id+"F78.opExtrude","CAP_FACE",FACE,{"disambiguationData":[OSD([sQuery(id+"F77.wireOp",EDGE,"E87"),sQuery(id+"F77.wireOp",EDGE,"E88.0"),sQuery(id+"F77.wireOp",EDGE,"E88.1"),sQuery(id+"F77.wireOp",EDGE,"E88.2"),sQuery(id+"F77.wireOp",EDGE,"E88.3"),sQuery(id+"F77.wireOp",EDGE,"E88.4"),sQuery(id+"F77.wireOp",EDGE,"E88.5")])],"isStart":false});
            var sketch = newSketch(context, id + "F82", { "sketchPlane" : qUnion([Q0])});
            skCircle(sketch, "E90", {"center": v(125.37, -39.5) * mm, "radius": 2.5 * mm});
            skSolve(sketch);
        }
        {
            var Q0;
            Q0=makeQuery(id+"F82.imprint","IMPRINT",FACE,{"disambiguationData":[TD([[makeQuery(id+"F82.imprint","IMPRINT",EDGE,{"derivedFrom":sQuery(id+"F82.wireOp",EDGE,"E90")}),1.0]])]});
            extrude(context, id + "F83", {"entities" : qUnion([Q0]), "operationType" : NewBodyOperationType.ADD, "depth" : 5 * mm, "offsetDistance" : 25 * mm});
        }
        {
            var Q0;
            Q0=qCreatedBy(makeId("Top.planeOp"),FACE);
            var sketch = newSketch(context, id + "F84", { "sketchPlane" : qUnion([Q0])});
            skCircle(sketch, "E91", {"center": v(100.05, -59.49) * mm, "radius": 2.5 * mm});
            skCircle(sketch, "E92", {"center": v(100.05, -59.49) * mm, "radius": 0.88 * mm});
            skSolve(sketch);
        }
        {
            var Q0;
            Q0 = qSketchRegion(id + "F84", true);
            extrude(context, id + "F85", {"entities" : qUnion([Q0]), "depth" : 27 * mm, "offsetDistance" : 25 * mm});
        }
        {
            var Q0;
            Q0=makeQuery(id+"F9.boolean.opBoolean","MERGE",FACE,{"derivedFrom":[makeQuery(id+"F7.opExtrude","CAP_FACE",FACE,{"disambiguationData":[OSD([sQuery(id+"F6.wireOp",EDGE,"E5")])],"isStart":false}),makeQuery(id+"F9.opExtrude","CAP_FACE",FACE,{"disambiguationData":[OSD([sQuery(id+"F8.wireOp",EDGE,"E6"),sQuery(id+"F8.wireOp",EDGE,"E7")])],"isStart":true})]});
            var sketch = newSketch(context, id + "F86", { "sketchPlane" : qUnion([Q0])});
            skCircle(sketch, "E93", {"center": v(-24.02, 11.3) * mm, "radius": 2.5 * mm});
            skSolve(sketch);
        }
        {
            var Q0;
            Q0=makeQuery(id+"F86.imprint","IMPRINT",FACE,{"disambiguationData":[TD([[makeQuery(id+"F86.imprint","IMPRINT",EDGE,{"derivedFrom":sQuery(id+"F86.wireOp",EDGE,"E93")}),1.0]])]});
            extrude(context, id + "F87", {"entities" : qUnion([Q0]), "operationType" : NewBodyOperationType.REMOVE, "oppositeDirection" : true, "depth" : 25 * mm, "offsetDistance" : 25 * mm});
        }
    });
